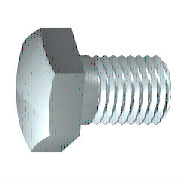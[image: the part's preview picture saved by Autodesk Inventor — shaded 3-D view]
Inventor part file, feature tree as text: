
AUTODESK INVENTOR PART (.ipt)
format: ipt  version: 2020 (Build 240168000, 168)  size: 197,120 bytes
history: native  units: mm (DEFAULTED — no unit token found)
features: sketch x3, extrude x1, chamfer x1, plane x1
ambient origin geometry x7: Origin, YZ Plane, XZ Plane, X Axis, Y Axis, Z Axis, Center Point
bodies: Solid1 (feature_tree), Body (feature_tree)
feature tree (6):
  extrude  "Head"  Depth=22.6mm
  chamfer  "Chamfer1"  Distance=3.0mm
  plane  "Work Plane1"
  sketch  "Sketch1"  dims[d0=25.0mm d1=22.6mm]
  sketch  "Sketch2"  dims[d2=5.0mm]
  sketch  "Sketch4"  dims[d12=90.0deg d3=3.0mm d4=0.0mm d5=30.0deg d21=90.0deg d6=0.49076mm d7=0.49086mm d8=0.0mm d9=0.5001mm d10=6.7mm d11=8.0mm d13=0.49086mm d14=4.566987mm d15=22.6mm d16=0.0mm d19=8.0mm d55=45.0deg d57=0.0mm d58=0.0mm]
